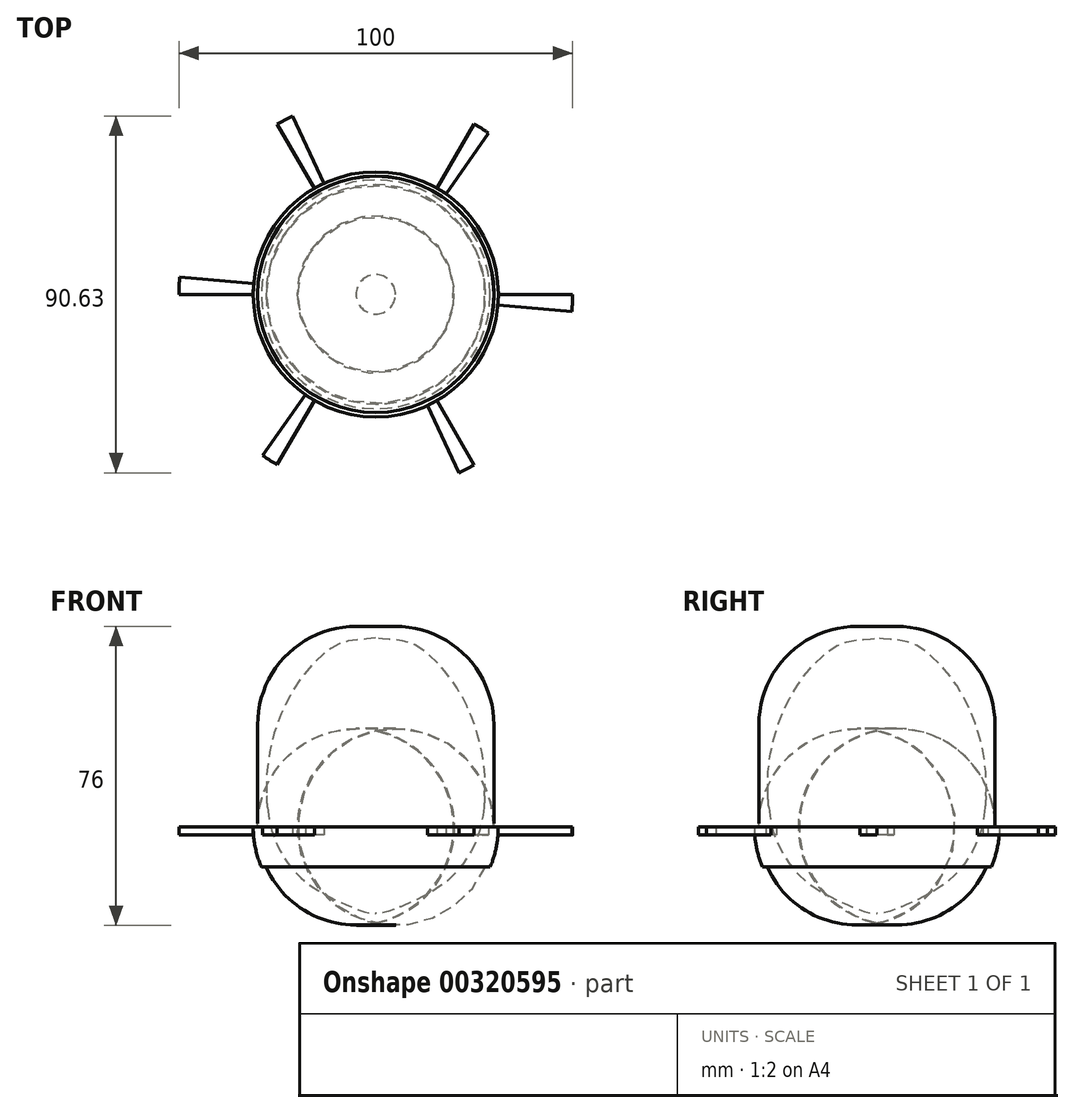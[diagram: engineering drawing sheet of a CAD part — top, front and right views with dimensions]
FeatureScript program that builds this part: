
annotation { "Feature Type Name" : "Feature", "Feature Type Description" : "" }
export const myFeature = defineFeature(function(context is Context, id is Id, definition is map)
    precondition{}
    {
        {
            var Q0;
            Q0=qCreatedBy(makeId("Front.planeOp"),FACE);
            var sketch = newSketch(context, id + "F0", { "sketchPlane" : qUnion([Q0])});
            skFitSpline(sketch, "E0", {"points": [v(0, 45.44) * mm, v(-8.86, 44.14) * mm, v(-16.29, 38.43) * mm, v(-20.86, 32.43) * mm, v(-25.14, 23.29) * mm, v(-27.43, 13.57) * mm, v(-27.71, 6.14) * mm, v(-26.29, -3.86) * mm, v(-22, -12.14) * mm, v(-16, -17.86) * mm, v(-6.57, -22.71) * mm, v(0, -24.56) * mm], "startDerivative": vector(-98.81, -15.48) * mm, "endDerivative": vector(79.6, -2.58) * mm});
            skLineSegment(sketch, "E1", {"start": v(0, 45.44) * mm, "end": v(0, -24.56) * mm});
            skPoint(sketch, "E2", {"position": v(-27.68, 5.4) * mm});
            skLineSegment(sketch, "E3", {"start": v(-30, 48.2) * mm, "end": v(-30, 5.4) * mm});
            skLineSegment(sketch, "E4", {"start": v(-30, -21.8) * mm, "end": v(-30, 2.4) * mm});
            skLineSegment(sketch, "E5", {"start": v(0, 45.44) * mm, "end": v(0, 48.44) * mm});
            skLineSegment(sketch, "E6", {"start": v(0, 48.44) * mm, "end": v(-30, 48.44) * mm});
            skLineSegment(sketch, "E7", {"start": v(-30, 48.44) * mm, "end": v(-30, 48.2) * mm});
            skLineSegment(sketch, "E8", {"start": v(0, -24.56) * mm, "end": v(0, -27.56) * mm});
            skLineSegment(sketch, "E9", {"start": v(0, -27.56) * mm, "end": v(-30, -27.56) * mm});
            skLineSegment(sketch, "E10", {"start": v(-30, -27.56) * mm, "end": v(-30, -21.8) * mm});
            skLineSegment(sketch, "E11", {"start": v(-30, 2.4) * mm, "end": v(-27.46, 2.4) * mm});
            skLineSegment(sketch, "E12", {"start": v(-30, 5.4) * mm, "end": v(-27.68, 5.4) * mm});
            skLineSegment(sketch, "E13", {"start": v(-30, 5.4) * mm, "end": v(-30, 2.4) * mm});
            skLineSegment(sketch, "E14", {"start": v(-30, 2.4) * mm, "end": v(-32, 2.4) * mm});
            skLineSegment(sketch, "E15", {"start": v(-32, 2.4) * mm, "end": v(-32, -27.56) * mm});
            skLineSegment(sketch, "E16", {"start": v(-32, -27.56) * mm, "end": v(-32, -29.56) * mm});
            skLineSegment(sketch, "E17", {"start": v(-32, -29.56) * mm, "end": v(0, -29.56) * mm});
            skLineSegment(sketch, "E18", {"start": v(0, -29.56) * mm, "end": v(0, -27.56) * mm});
            skSolve(sketch);
        }
        {
            var Q0;
            Q0=makeQuery(id+"F0.imprint","IMPRINT",FACE,{"disambiguationData":[TD([[makeQuery(id+"F0.imprint","IMPRINT",EDGE,{"derivedFrom":sQuery(id+"F0.wireOp",EDGE,"E3")}),1.0]])]});
            var Q1;
            {var subQ0=sQuery(id+"F0.wireOp",EDGE,"E11");Q1=makeQuery(id+"F0.imprint","IMPRINT",FACE,{"disambiguationData":[TD([[makeQuery(id+"F0.imprint","IMPRINT",EDGE,{"derivedFrom":subQ0}),1.0]])]});}
            var Q2;
            Q2=makeQuery(id+"F0.imprint","IMPRINT",FACE,{"disambiguationData":[TD([[makeQuery(id+"F0.imprint","IMPRINT",EDGE,{"derivedFrom":sQuery(id+"F0.wireOp",EDGE,"E4")}),-1.0]])]});
            var Q3;
            Q3=sQuery(id+"F0.wireOp",EDGE,"E1");
            revolve(context, id + "F1", {"entities" : qUnion([Q0, Q1, Q2]), "axis" : qUnion([Q3]), "revolveType" : RevolveType.FULL});
        }
        {
            var Q0;
            Q0=makeQuery(id+"F1.opRevolve","SWEPT_EDGE",EDGE,{"disambiguationData":[OSD([sQuery(id+"F0.wireOp",EDGE,"E6"),sQuery(id+"F0.wireOp",EDGE,"E7")])]});
            fillet(context, id + "F2", {"entities" : qUnion([Q0]), "radius" : 25 * mm, "tangentPropagation" : true, "allowEdgeOverflow" : false});
        }
        {
            var Q0;
            Q0=makeQuery(id+"F1.opRevolve","SWEPT_FACE",FACE,{"disambiguationData":[OSD([sQuery(id+"F0.wireOp",EDGE,"E3"),sQuery(id+"F0.wireOp",EDGE,"E4"),sQuery(id+"F0.wireOp",EDGE,"E7"),sQuery(id+"F0.wireOp",EDGE,"E10"),sQuery(id+"F0.wireOp",EDGE,"E13")])]});
            fillet(context, id + "F3", {"entities" : qUnion([Q0]), "radius" : 25 * mm, "tangentPropagation" : true, "allowEdgeOverflow" : false});
        }
        {
            var Q0;
            Q0=qCreatedBy(makeId("Front.planeOp"),FACE);
            var sketch = newSketch(context, id + "F4", { "sketchPlane" : qUnion([Q0])});
            skLineSegment(sketch, "E19", {"start": v(-30.06, -2.56) * mm, "end": v(-32.32, -2.56) * mm});
            skLineSegment(sketch, "E20", {"start": v(-30, 0.5) * mm, "end": v(-30, -3.6) * mm});
            skLineSegment(sketch, "E21", {"start": v(-30, -2.56) * mm, "end": v(-5.14, -2.56) * mm});
            skCircle(sketch, "E22", {"center": v(-5.14, -2.56) * mm, "radius": 24.92 * mm});
            skLineSegment(sketch, "E23", {"start": v(-5.14, -2.56) * mm, "end": v(-5.14, -27.48) * mm});
            skLineSegment(sketch, "E24", {"start": v(-5.14, -2.56) * mm, "end": v(0, -2.56) * mm});
            skLineSegment(sketch, "E25", {"start": v(0, -2.56) * mm, "end": v(5.14, -2.56) * mm});
            skCircle(sketch, "E26", {"center": v(5.14, -2.56) * mm, "radius": 24.88 * mm});
            skLineSegment(sketch, "E27", {"start": v(-5.14, -27.48) * mm, "end": v(5.23, -27.44) * mm});
            skLineSegment(sketch, "E28", {"start": v(-32.32, -2.56) * mm, "end": v(33.8, -2.56) * mm});
            skCircle(sketch, "E29", {"center": v(-5.14, -2.56) * mm, "radius": 26 * mm});
            skCircle(sketch, "E30", {"center": v(5.14, -2.56) * mm, "radius": 26 * mm});
            skLineSegment(sketch, "E31", {"start": v(-5.14, -28.56) * mm, "end": v(5.23, -28.56) * mm});
            skLineSegment(sketch, "E32", {"start": v(0, -27.46) * mm, "end": v(0, -28.56) * mm});
            skPoint(sketch, "E32.startSnap0", {"position": v(0.05, -27.46) * mm});
            skPoint(sketch, "E32.endSnap0", {"position": v(0.05, -28.56) * mm});
            skLineSegment(sketch, "E33", {"start": v(29.06, -12.74) * mm, "end": v(27.84, -12.74) * mm});
            skLineSegment(sketch, "E34", {"start": v(-27.88, -12.74) * mm, "end": v(-29.06, -12.74) * mm});
            skSolve(sketch);
        }
        {
            var Q0;
            {var subQ0=sQuery(id+"F4.wireOp",EDGE,"E33");Q0=makeQuery(id+"F4.imprint","IMPRINT",FACE,{"disambiguationData":[TD([[makeQuery(id+"F4.imprint","IMPRINT",EDGE,{"derivedFrom":subQ0}),-1.0]])]});}
            var Q1;
            Q1=sQuery(id+"F0.wireOp",EDGE,"E1");
            revolve(context, id + "F5", {"entities" : qUnion([Q0]), "axis" : qUnion([Q1]), "revolveType" : RevolveType.FULL});
        }
        {
            var Q0;
            Q0=makeQuery(id+"F5.opRevolve","SWEPT_FACE",FACE,{"disambiguationData":[OSD([sQuery(id+"F4.wireOp",EDGE,"E28")])]});
            var sketch = newSketch(context, id + "F6", { "sketchPlane" : qUnion([Q0])});
            skLineSegment(sketch, "E35", {"start": v(31.14, 0) * mm, "end": v(50, 0) * mm});
            skLineSegment(sketch, "E36", {"start": v(15.53, -26.98) * mm, "end": v(24.97, -43.32) * mm});
            skLineSegment(sketch, "E37", {"start": v(-15.6, -26.94) * mm, "end": v(-25.03, -43.28) * mm});
            skLineSegment(sketch, "E38", {"start": v(15.53, 26.98) * mm, "end": v(24.97, 43.32) * mm});
            skLineSegment(sketch, "E39", {"start": v(-15.6, 26.94) * mm, "end": v(-25.03, 43.28) * mm});
            skLineSegment(sketch, "E40", {"start": v(-31.14, 0) * mm, "end": v(-50, 0) * mm});
            skSolve(sketch);
        }
        {
            var Q0;
            Q0=sQuery(id+"F6.wireOp",EDGE,"E36");
            var Q1;
            Q1=sQuery(id+"F6.wireOp",EDGE,"E37");
            var Q2;
            Q2=sQuery(id+"F6.wireOp",EDGE,"E40");
            var Q3;
            Q3=sQuery(id+"F6.wireOp",EDGE,"E39");
            var Q4;
            Q4=sQuery(id+"F6.wireOp",EDGE,"E38");
            var Q5;
            Q5=sQuery(id+"F6.wireOp",EDGE,"E35");
            extrude(context, id + "F7", {"bodyType" : ToolBodyType.SURFACE, "surfaceEntities" : qUnion([Q0, Q1, Q2, Q3, Q4, Q5]), "oppositeDirection" : true, "depth" : 2 * mm});
        }
        {
            var Q0;
            Q0=makeQuery(id+"F7.opExtrude","SWEPT_FACE",FACE,{"disambiguationData":[OSD([sQuery(id+"F6.wireOp",EDGE,"E36")])]});
            var Q1;
            Q1=makeQuery(id+"F7.opExtrude","SWEPT_FACE",FACE,{"disambiguationData":[OSD([sQuery(id+"F6.wireOp",EDGE,"E35")])]});
            var Q2;
            Q2=makeQuery(id+"F7.opExtrude","SWEPT_FACE",FACE,{"disambiguationData":[OSD([sQuery(id+"F6.wireOp",EDGE,"E38")])]});
            var Q3;
            Q3=makeQuery(id+"F7.opExtrude","SWEPT_FACE",FACE,{"disambiguationData":[OSD([sQuery(id+"F6.wireOp",EDGE,"E39")])]});
            var Q4;
            Q4=makeQuery(id+"F7.opExtrude","SWEPT_FACE",FACE,{"disambiguationData":[OSD([sQuery(id+"F6.wireOp",EDGE,"E40")])]});
            var Q5;
            Q5=makeQuery(id+"F7.opExtrude","SWEPT_FACE",FACE,{"disambiguationData":[OSD([sQuery(id+"F6.wireOp",EDGE,"E37")])]});
            var Q6;
            Q6=sQuery(id+"F0.wireOp",EDGE,"E1");
            revolve(context, id + "F8", {"operationType" : NewBodyOperationType.ADD, "entities" : qUnion([Q0, Q1, Q2, Q3, Q4, Q5]), "axis" : qUnion([Q6]), "revolveType" : RevolveType.ONE_DIRECTION, "angle" : 5 * degree});
        }
    });
